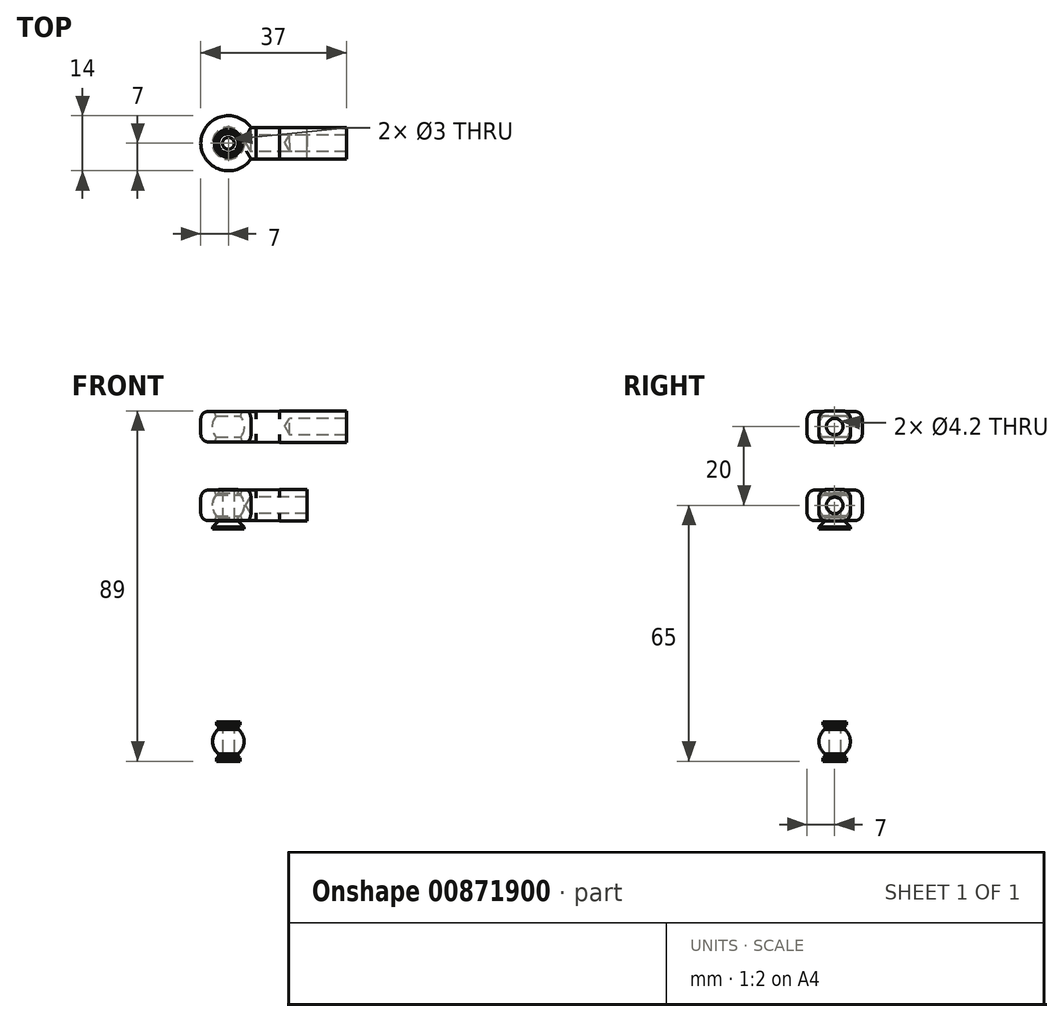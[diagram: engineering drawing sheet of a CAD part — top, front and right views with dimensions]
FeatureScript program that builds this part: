
annotation { "Feature Type Name" : "Feature", "Feature Type Description" : "" }
export const myFeature = defineFeature(function(context is Context, id is Id, definition is map)
    precondition{}
    {
        {
            var Q0;
            Q0=qCreatedBy(makeId("Front.planeOp"),FACE);
            var sketch = newSketch(context, id + "F0", { "sketchPlane" : qUnion([Q0])});
            skArc(sketch, "E0", {"start": v(2.5, -3.12) * mm, "mid": v(4, 0) * mm, "end": v(2.5, 3.12) * mm});
            skLineSegment(sketch, "E1", {"start": v(1.5, 4) * mm, "end": v(2.5, 4) * mm});
            skLineSegment(sketch, "E2", {"start": v(2.5, 4) * mm, "end": v(2.5, 3.12) * mm});
            skLineSegment(sketch, "E3", {"start": v(1.5, 4) * mm, "end": v(1.5, -6) * mm});
            skLineSegment(sketch, "E4", {"start": v(2.5, -4) * mm, "end": v(1.5, -4) * mm, "construction": true});
            skLineSegment(sketch, "E5.trimOffspring", {"start": v(2.5, -3.12) * mm, "end": v(2.5, -4) * mm});
            skLineSegment(sketch, "E6", {"start": v(0, 0) * mm, "end": v(0, 7.62) * mm, "construction": true});
            skLineSegment(sketch, "E7", {"start": v(0, 0) * mm, "end": v(8.34, 0) * mm, "construction": true});
            skPoint(sketch, "E7.endSnap0", {"position": v(1.5, 0) * mm});
            skLineSegment(sketch, "E8", {"start": v(2.5, -4) * mm, "end": v(4, -6) * mm, "construction": true});
            skLineSegment(sketch, "E9", {"start": v(4, -6) * mm, "end": v(1.5, -6) * mm});
            skPoint(sketch, "E10.orphan", {"position": v(0, -6) * mm});
            skLineSegment(sketch, "E11", {"start": v(4, -6) * mm, "end": v(4, -5.5) * mm});
            skLineSegment(sketch, "E12", {"start": v(4, -5.5) * mm, "end": v(2.5, -4) * mm});
            skSolve(sketch);
        }
        {
            var Q0;
            Q0=qSketchRegion(id+"F0",true);
            var Q1;
            Q1=sQuery(id+"F0.wireOp",EDGE,"E6");
            revolve(context, id + "F1", {"surfaceOperationType" : NewSurfaceOperationType.NEW, "entities" : qUnion([Q0]), "axis" : qUnion([Q1]), "revolveType" : RevolveType.FULL});
        }
        {
            var Q0;
            Q0=qCreatedBy(makeId("Front.planeOp"),FACE);
            var sketch = newSketch(context, id + "F2", { "sketchPlane" : qUnion([Q0])});
            skArc(sketch, "E13.0", {"start": v(3.1, -2.68) * mm, "mid": v(4.1, 0) * mm, "end": v(3.1, 2.68) * mm});
            skLineSegment(sketch, "E14", {"start": v(3.55, 3.9) * mm, "end": v(7, 3.9) * mm});
            skLineSegment(sketch, "E15", {"start": v(7, 3.9) * mm, "end": v(7, -3.9) * mm});
            skLineSegment(sketch, "E16", {"start": v(7, -3.9) * mm, "end": v(3.55, -3.9) * mm});
            skLineSegment(sketch, "E17", {"start": v(0, 0) * mm, "end": v(2.53, 6.95) * mm, "construction": true});
            skLineSegment(sketch, "E18", {"start": v(0, 0) * mm, "end": v(2.64, -7.26) * mm, "construction": true});
            skLineSegment(sketch, "E19.trimOffspring", {"start": v(3.1, -2.68) * mm, "end": v(3.55, -3.9) * mm});
            skLineSegment(sketch, "E20.trimOffspring", {"start": v(3.1, 2.68) * mm, "end": v(3.55, 3.9) * mm});
            skSolve(sketch);
        }
        {
            var Q0;
            Q0=qSketchRegion(id+"F2",true);
            var Q1;
            Q1=sQuery(id+"F0.wireOp",EDGE,"E6");
            revolve(context, id + "F3", {"surfaceOperationType" : NewSurfaceOperationType.NEW, "entities" : qUnion([Q0]), "axis" : qUnion([Q1]), "revolveType" : RevolveType.FULL});
        }
        {
            var Q0;
            Q0=qCreatedBy(makeId("Front.planeOp"),FACE);
            var sketch = newSketch(context, id + "F4", { "sketchPlane" : qUnion([Q0])});
            skLineSegment(sketch, "E21.bottom", {"start": v(13, 4) * mm, "end": v(20, 4) * mm});
            skLineSegment(sketch, "E21.top", {"start": v(13, -4) * mm, "end": v(20, -4) * mm});
            skLineSegment(sketch, "E21.left", {"start": v(13, 4) * mm, "end": v(13, -4) * mm, "construction": true});
            skLineSegment(sketch, "E21.right", {"start": v(20, 4) * mm, "end": v(20, -4) * mm});
            skPoint(sketch, "E21.middle", {"position": v(16.5, 0) * mm});
            skLineSegment(sketch, "E22", {"start": v(7, 3.9) * mm, "end": v(7, -3.9) * mm, "construction": true});
            skLineSegment(sketch, "E23", {"start": v(13, 4) * mm, "end": v(7, 3.9) * mm});
            skLineSegment(sketch, "E24", {"start": v(13, -4) * mm, "end": v(7, -3.9) * mm});
            skLineSegment(sketch, "E25", {"start": v(5, -3.9) * mm, "end": v(5, 3.9) * mm});
            skLineSegment(sketch, "E26", {"start": v(5, 3.9) * mm, "end": v(7, 3.9) * mm});
            skLineSegment(sketch, "E27", {"start": v(5, -3.9) * mm, "end": v(7, -3.9) * mm});
            skSolve(sketch);
        }
        {
            var Q0;
            Q0=qSketchRegion(id+"F4",true);
            extrude(context, id + "F5", {"entities" : qUnion([Q0]), "operationType" : NewBodyOperationType.ADD, "depth" : 8 * mm, "offsetDistance" : 25 * mm, "symmetric" : true});
        }
        {
            var Q0;
            Q0=makeQuery(id+"F5.opExtrude","CAP_EDGE",EDGE,{"disambiguationData":[OSD([sQuery(id+"F4.wireOp",EDGE,"E21.bottom")])],"isStart":false});
            var Q1;
            Q1=makeQuery(id+"F3.opRevolve","SWEPT_EDGE",EDGE,{"disambiguationData":[OSD([sQuery(id+"F2.wireOp",EDGE,"E14"),sQuery(id+"F2.wireOp",EDGE,"E15")])]});
            var Q2;
            Q2=makeQuery(id+"F5.opExtrude","CAP_EDGE",EDGE,{"disambiguationData":[OSD([sQuery(id+"F4.wireOp",EDGE,"E21.bottom")])],"isStart":true});
            var Q3;
            Q3=makeQuery(id+"F5.opExtrude","CAP_EDGE",EDGE,{"disambiguationData":[OSD([sQuery(id+"F4.wireOp",EDGE,"E21.top")])],"isStart":true});
            var Q4;
            Q4=makeQuery(id+"F3.opRevolve","SWEPT_EDGE",EDGE,{"disambiguationData":[OSD([sQuery(id+"F2.wireOp",EDGE,"E15"),sQuery(id+"F2.wireOp",EDGE,"E16")])]});
            var Q5;
            Q5=makeQuery(id+"F5.opExtrude","CAP_EDGE",EDGE,{"disambiguationData":[OSD([sQuery(id+"F4.wireOp",EDGE,"E21.top")])],"isStart":false});
            fillet(context, id + "F6", {"entities" : qUnion([Q0, Q1, Q2, Q3, Q4, Q5]), "radius" : 2 * mm, "tangentPropagation" : true, "allowEdgeOverflow" : false});
        }
        {
            var Q0;
            Q0=makeQuery(id+"F5.opExtrude","SWEPT_FACE",FACE,{"disambiguationData":[OSD([sQuery(id+"F4.wireOp",EDGE,"E21.right")])]});
            var sketch = newSketch(context, id + "F7", { "sketchPlane" : qUnion([Q0])});
            skPoint(sketch, "E28", {"position": v(0, 0) * mm});
            skSolve(sketch);
        }
        {
            var Q0;
            Q0=makeQuery(id+"F3.opRevolve","SWEPT_BODY",BODY,{"disambiguationData":[OSD([sQuery(id+"F2.wireOp",EDGE,"E13.0"),sQuery(id+"F2.wireOp",EDGE,"E14"),sQuery(id+"F2.wireOp",EDGE,"E15"),sQuery(id+"F2.wireOp",EDGE,"E16"),sQuery(id+"F2.wireOp",EDGE,"E19.trimOffspring"),sQuery(id+"F2.wireOp",EDGE,"E20.trimOffspring")])]});
            transform(context, id + "F8", {"entities" : qUnion([Q0]), "transformType" : TransformType.TRANSLATION_3D, "dx" : 0 * mm, "dy" : 0 * mm, "dz" : 20 * mm, "makeCopy" : true});
        }
        {
            var Q0;
            Q0=makeQuery(id+"F8.opPattern","COPY",FACE,{"derivedFrom":makeQuery(id+"F5.opExtrude","SWEPT_FACE",FACE,{"disambiguationData":[OSD([sQuery(id+"F4.wireOp",EDGE,"E21.right")])]}),"instanceName":"1"});
            extrude(context, id + "F9", {"entities" : qUnion([Q0]), "operationType" : NewBodyOperationType.ADD, "depth" : 10 * mm, "offsetDistance" : 25 * mm});
        }
        {
            var Q0;
            Q0=makeQuery(id+"F9.opExtrude","CAP_FACE",FACE,{"disambiguationData":[OSD([sQuery(id+"F4.wireOp",EDGE,"E21.right")])],"isStart":false});
            var sketch = newSketch(context, id + "F10", { "sketchPlane" : qUnion([Q0])});
            skPoint(sketch, "E29", {"position": v(0, 20) * mm});
            skPoint(sketch, "E29.positionSnap0", {"position": v(4, 20) * mm});
            skPoint(sketch, "E29.positionSnap1", {"position": v(0, 24) * mm});
            skSolve(sketch);
        }
        {
            var Q0;
            Q0=sQuery(id+"F10.wireOp",VERTEX,"E29");
            var Q1;
            Q1=sQuery(id+"F7.wireOp",VERTEX,"E28");
            var Q2;
            Q2=makeQuery(id+"F3.opRevolve","SWEPT_BODY",BODY,{"disambiguationData":[OSD([sQuery(id+"F2.wireOp",EDGE,"E13.0"),sQuery(id+"F2.wireOp",EDGE,"E14"),sQuery(id+"F2.wireOp",EDGE,"E15"),sQuery(id+"F2.wireOp",EDGE,"E16"),sQuery(id+"F2.wireOp",EDGE,"E19.trimOffspring"),sQuery(id+"F2.wireOp",EDGE,"E20.trimOffspring")])]});
            var Q3;
            Q3=makeQuery(id+"F8.opPattern","COPY",BODY,{"derivedFrom":makeQuery(id+"F3.opRevolve","SWEPT_BODY",BODY,{"disambiguationData":[OSD([sQuery(id+"F2.wireOp",EDGE,"E13.0"),sQuery(id+"F2.wireOp",EDGE,"E14"),sQuery(id+"F2.wireOp",EDGE,"E15"),sQuery(id+"F2.wireOp",EDGE,"E16"),sQuery(id+"F2.wireOp",EDGE,"E19.trimOffspring"),sQuery(id+"F2.wireOp",EDGE,"E20.trimOffspring")])]}),"instanceName":"1"});
            hole(context, id + "F11", {"style" : HoleStyle.SIMPLE, "endStyle" : HoleEndStyle.BLIND, "standardTappedOrClearance" : lookupTablePath({ "standard" : "ISO", "engagement" : "75%", "pitch" : "0.8 mm", "size" : "M5", "type" : "Tapped" }), "standardBlindInLast" : lookupTablePath({ "standard" : "ISO", "engagement" : "75%", "pitch" : "0.8 mm", "size" : "M5", "type" : "Tapped" }), "holeDiameter" : 4.2 * mm, "majorDiameter" : 5 * mm, "showTappedDepth" : true, "holeDepth" : 14.4 * mm, "isTappedThrough" : true, "tappedDepth" : 12 * mm, "tapClearance" : 3, "locations" : qUnion([Q0, Q1]), "scope" : qUnion([Q2, Q3])});
        }
        {
            var Q0;
            Q0=qCreatedBy(makeId("Front.planeOp"),FACE);
            var sketch = newSketch(context, id + "F12", { "sketchPlane" : qUnion([Q0])});
            skArc(sketch, "E30", {"start": v(2.5, -63.12) * mm, "mid": v(4, -60) * mm, "end": v(2.5, -56.88) * mm});
            skLineSegment(sketch, "E31", {"start": v(1.5, -56) * mm, "end": v(2.5, -56) * mm, "construction": true});
            skLineSegment(sketch, "E32", {"start": v(2.5, -56) * mm, "end": v(2.5, -56.88) * mm});
            skLineSegment(sketch, "E33", {"start": v(1.5, -55) * mm, "end": v(1.5, -65) * mm});
            skLineSegment(sketch, "E34", {"start": v(2.5, -64) * mm, "end": v(1.5, -64) * mm, "construction": true});
            skLineSegment(sketch, "E35.trimOffspring", {"start": v(2.5, -63.12) * mm, "end": v(2.5, -64) * mm});
            skLineSegment(sketch, "E36", {"start": v(0, -60) * mm, "end": v(0, -14.76) * mm, "construction": true});
            skLineSegment(sketch, "E37", {"start": v(-42.77, -60) * mm, "end": v(0, -60) * mm, "construction": true});
            skPoint(sketch, "E37.endSnap0", {"position": v(1.5, -60) * mm});
            skLineSegment(sketch, "E38", {"start": v(2.5, -64) * mm, "end": v(3, -64.2) * mm});
            skLineSegment(sketch, "E39", {"start": v(3, -64.2) * mm, "end": v(3, -65) * mm});
            skLineSegment(sketch, "E40", {"start": v(3, -65) * mm, "end": v(1.5, -65) * mm});
            skLineSegment(sketch, "E41", {"start": v(2.5, -56) * mm, "end": v(3, -55.8) * mm});
            skLineSegment(sketch, "E42", {"start": v(3, -55.8) * mm, "end": v(3, -55) * mm});
            skLineSegment(sketch, "E43", {"start": v(3, -55) * mm, "end": v(1.5, -55) * mm});
            skPoint(sketch, "E44.orphan", {"position": v(0, -65) * mm});
            skSolve(sketch);
        }
        {
            var Q0;
            Q0=makeQuery(id+"F12.imprint","IMPRINT",FACE,{"disambiguationData":[TD([[makeQuery(id+"F12.imprint","IMPRINT",EDGE,{"derivedFrom":sQuery(id+"F12.wireOp",EDGE,"E30")}),1.0]])]});
            var Q1;
            Q1=sQuery(id+"F12.wireOp",EDGE,"E36");
            revolve(context, id + "F13", {"surfaceOperationType" : NewSurfaceOperationType.NEW, "entities" : qUnion([Q0]), "axis" : qUnion([Q1]), "revolveType" : RevolveType.FULL});
        }
    });
